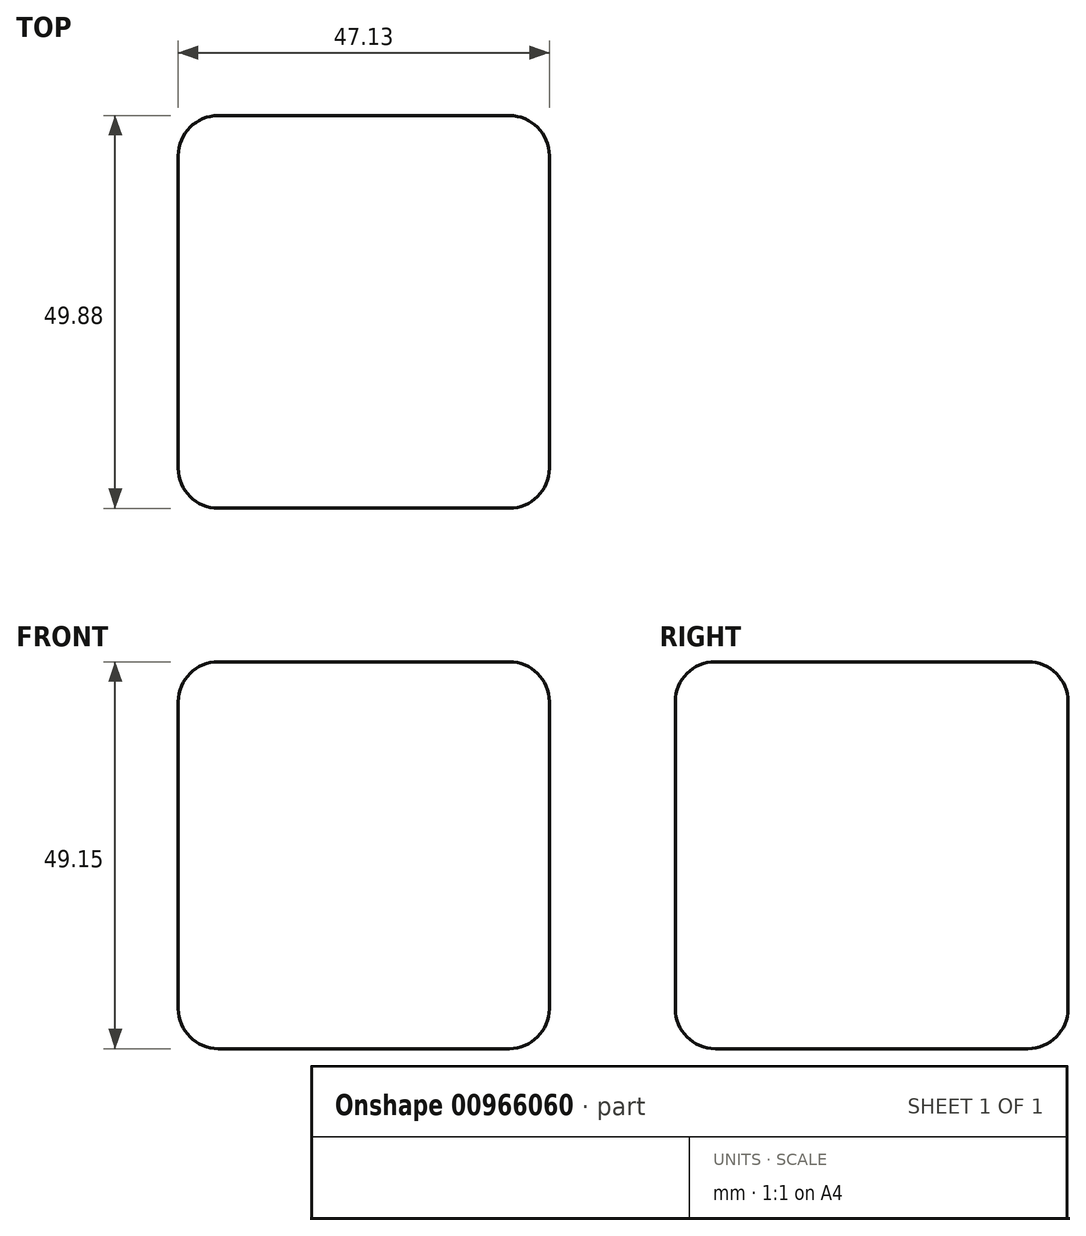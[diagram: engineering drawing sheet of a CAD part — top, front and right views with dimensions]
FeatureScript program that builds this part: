
annotation { "Feature Type Name" : "Feature", "Feature Type Description" : "" }
export const myFeature = defineFeature(function(context is Context, id is Id, definition is map)
    precondition{}
    {
        {
            var Q0;
            Q0=qCreatedBy(makeId("Top.planeOp"),FACE);
            var sketch = newSketch(context, id + "F0", { "sketchPlane" : qUnion([Q0])});
            skLineSegment(sketch, "E0.bottom", {"start": v(30.57, -29.86) * mm, "end": v(-16.56, -29.86) * mm});
            skLineSegment(sketch, "E0.top", {"start": v(30.57, 20.02) * mm, "end": v(-16.56, 20.02) * mm});
            skLineSegment(sketch, "E0.left", {"start": v(30.57, -29.86) * mm, "end": v(30.57, 20.02) * mm});
            skLineSegment(sketch, "E0.right", {"start": v(-16.56, -29.86) * mm, "end": v(-16.56, 20.02) * mm});
            skSolve(sketch);
        }
        {
            var Q0;
            Q0=makeQuery(id+"F0.imprint","IMPRINT",FACE,{"disambiguationData":[TD([[makeQuery(id+"F0.imprint","IMPRINT",EDGE,{"derivedFrom":sQuery(id+"F0.wireOp",EDGE,"E0.bottom")}),-1.0]])]});
            extrude(context, id + "F1", {"entities" : qUnion([Q0]), "depth" : 49.15 * mm, "offsetDistance" : 25.4 * mm});
        }
        {
            var Q1;
            Q1=makeQuery(id+"F1.opExtrude","CAP_FACE",FACE,{"disambiguationData":[OSD([sQuery(id+"F0.wireOp",EDGE,"E0.bottom"),sQuery(id+"F0.wireOp",EDGE,"E0.top"),sQuery(id+"F0.wireOp",EDGE,"E0.left"),sQuery(id+"F0.wireOp",EDGE,"E0.right")])],"isStart":true});
            var Q2;
            Q2=makeQuery(id+"F1.opExtrude","CAP_FACE",FACE,{"disambiguationData":[OSD([sQuery(id+"F0.wireOp",EDGE,"E0.bottom"),sQuery(id+"F0.wireOp",EDGE,"E0.top"),sQuery(id+"F0.wireOp",EDGE,"E0.left"),sQuery(id+"F0.wireOp",EDGE,"E0.right")])],"isStart":false});
            loft(context, id + "F2", {"operationType" : NewBodyOperationType.ADD, "sheetProfilesArray" : [{ "sheetProfileEntities" : qUnion([Q1]) }, { "sheetProfileEntities" : qUnion([Q2]) }]});
        }
        {
            var Q0;
            Q0=makeQuery(id+"F1.opExtrude","CAP_EDGE",EDGE,{"disambiguationData":[OSD([sQuery(id+"F0.wireOp",EDGE,"E0.top")])],"isStart":false});
            var Q1;
            Q1=makeQuery(id+"F1.opExtrude","CAP_EDGE",EDGE,{"disambiguationData":[OSD([sQuery(id+"F0.wireOp",EDGE,"E0.right")])],"isStart":false});
            var Q2;
            Q2=makeQuery(id+"F1.opExtrude","CAP_EDGE",EDGE,{"disambiguationData":[OSD([sQuery(id+"F0.wireOp",EDGE,"E0.top")])],"isStart":true});
            var Q3;
            Q3=makeQuery(id+"F1.opExtrude","CAP_EDGE",EDGE,{"disambiguationData":[OSD([sQuery(id+"F0.wireOp",EDGE,"E0.right")])],"isStart":true});
            var Q4;
            Q4=makeQuery(id+"F1.opExtrude","SWEPT_EDGE",EDGE,{"disambiguationData":[OSD([sQuery(id+"F0.wireOp",EDGE,"E0.top"),sQuery(id+"F0.wireOp",EDGE,"E0.right")])]});
            var Q5;
            Q5=makeQuery(id+"F1.opExtrude","CAP_EDGE",EDGE,{"disambiguationData":[OSD([sQuery(id+"F0.wireOp",EDGE,"E0.bottom")])],"isStart":false});
            var Q6;
            Q6=makeQuery(id+"F1.opExtrude","CAP_EDGE",EDGE,{"disambiguationData":[OSD([sQuery(id+"F0.wireOp",EDGE,"E0.left")])],"isStart":false});
            var Q7;
            Q7=makeQuery(id+"F1.opExtrude","SWEPT_FACE",FACE,{"disambiguationData":[OSD([sQuery(id+"F0.wireOp",EDGE,"E0.bottom")])]});
            var Q8;
            Q8=makeQuery(id+"F1.opExtrude","SWEPT_EDGE",EDGE,{"disambiguationData":[OSD([sQuery(id+"F0.wireOp",EDGE,"E0.top"),sQuery(id+"F0.wireOp",EDGE,"E0.left")])]});
            var Q9;
            Q9=makeQuery(id+"F1.opExtrude","CAP_EDGE",EDGE,{"disambiguationData":[OSD([sQuery(id+"F0.wireOp",EDGE,"E0.left")])],"isStart":true});
            fillet(context, id + "F3", {"entities" : qUnion([Q0, Q1, Q2, Q3, Q4, Q5, Q6, Q7, Q8, Q9]), "radius" : 5.08 * mm, "tangentPropagation" : true, "allowEdgeOverflow" : false});
        }
    });
